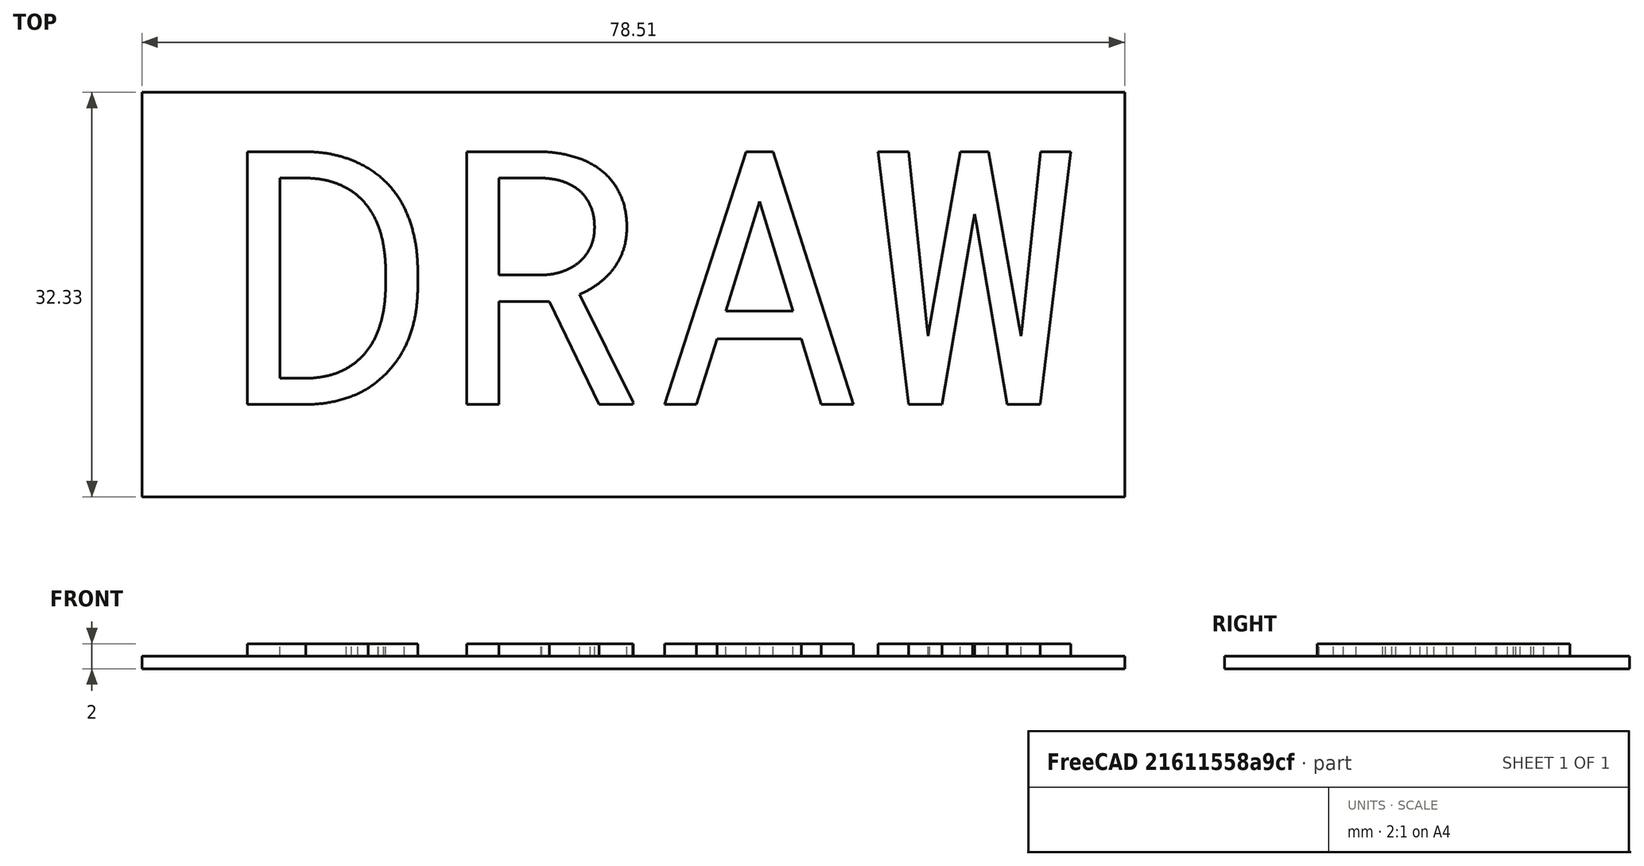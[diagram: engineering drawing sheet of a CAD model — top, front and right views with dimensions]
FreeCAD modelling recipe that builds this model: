
FCSTD DOCUMENT  (FreeCAD 0.19R24291 (Git))
Label: text-inlay
License: All rights reserved
LicenseURL: http://en.wikipedia.org/wiki/All_rights_reserved
objects: PartDesign::Pad×2, Part::Part2DObjectPython×1, Sketcher::SketchObject×1, PartDesign::Body×1
note: 7 computed .brp shape members not serialized (recipe doc carries the construction recipe); baked Part::Feature solids carry a one-line shape summary decoded from their .brp

FEATURE [Part::Part2DObjectPython] ShapeString  # Draft 2D object (typed FeaturePython)
  FontFile = <userpath>/feeder/lib/fonts/RobotoMono-VariableFont_weight.ttf
  Placement = pos=(-58.79,-47.9,0) rot=(0,0,1;0rad)
  Size = 25
  String = DRAW
  Tracking = 0
FEATURE [Sketcher::SketchObject] Sketch
  FullyConstrained = false
  MapMode = 5
  Support = -> [XY_Plane]
  sketch-geometry (4):
    g0: LineSegment StartX=-65.0472 StartY=-22.9435 StartZ=0 EndX=13.4621 EndY=-22.9435 EndZ=0
    g1: LineSegment StartX=13.4621 StartY=-22.9435 StartZ=0 EndX=13.4621 EndY=-55.2709 EndZ=0
    g2: LineSegment StartX=13.4621 StartY=-55.2709 StartZ=0 EndX=-65.0472 EndY=-55.2709 EndZ=0
    g3: LineSegment StartX=-65.0472 StartY=-55.2709 StartZ=0 EndX=-65.0472 EndY=-22.9435 EndZ=0
  constraints (8):
    c: Coincident(g0,g1)
    c: Coincident(g1,g2)
    c: Coincident(g2,g3)
    c: Coincident(g3,g0)
    c: Horizontal(g0)
    c: Horizontal(g2)
    c: Vertical(g1)
    c: Vertical(g3)
FEATURE [PartDesign::Pad] Pad
  Direction = (1,1,1)
  Length = 1
  Length2 = 100
  Profile = -> Sketch
  Reversed = true
  Type = 0
FEATURE [PartDesign::Pad] Pad001
  BaseFeature = -> Pad
  Direction = (1,1,1)
  Length = 1
  Length2 = 100
  Profile = -> ShapeString
  Type = 0
FEATURE [PartDesign::Body] Body
  Group = -> [ShapeString,Sketch,Pad,Pad001]
  Origin = -> Origin
  Tip = -> Pad001
